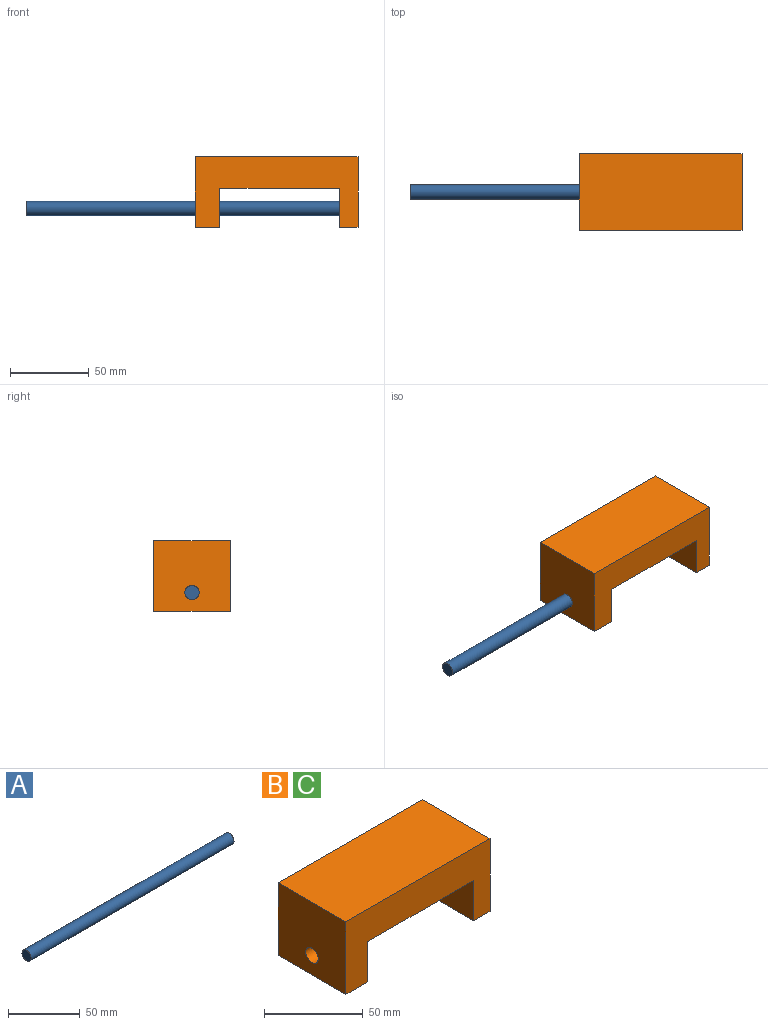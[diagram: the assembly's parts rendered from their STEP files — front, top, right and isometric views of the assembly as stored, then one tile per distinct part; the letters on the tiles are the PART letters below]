
ASSEMBLY  parts=3 mates=1
PART A: 3 faces, bbox 200x9x9 mm
  f0: cylinder r=4.5mm len=200mm, axis (1,0,0), area 5654.9mm2, adj f1,f2
  f1: plane 9x9mm, normal (-1,0,0), area 63.6mm2, adj f0
  f2: plane 9x9mm, normal (1,0,0), area 63.6mm2, adj f0
PART B: 11 faces, bbox 103.2x48.6x45 mm
  f0: plane 75.82x48.64mm, normal (0,0,-1), area 3687.7mm2, adj f1,f3,f6,f9
  f1: plane 103.2x45mm, normal (0,1,0), area 2748.6mm2, adj f0,f2,f4,f5,f6,f7,f9,f10
  f2: plane 48.64x45mm, normal (-1,0,0), area 2125mm2, adj f1,f3,f5,f7,f8
  f3: plane 103.2x45mm, normal (0,-1,0), area 2748.6mm2, adj f0,f2,f4,f5,f6,f7,f9,f10
  f4: plane 48.64x45mm, normal (1,0,0), area 2188.6mm2, adj f1,f3,f5,f10
  f5: plane 103.2x48.64mm, normal (0,0,1), area 5019.5mm2, adj f1,f2,f3,f4
  f6: plane 48.64x25mm, normal (1,0,0), area 1152.3mm2, adj f0,f1,f3,f7,f8
  f7: plane 48.64x15.58mm, normal (0,0,-1), area 757.7mm2, adj f1,f2,f3,f6
  f8: cylinder r=4.5mm len=15.58mm, axis (-1,0,0), area 440.5mm2, adj f2,f6
  f9: plane 48.64x25mm, normal (-1,0,0), area 1215.9mm2, adj f0,f1,f3,f10
  f10: plane 48.64x11.8mm, normal (0,0,-1), area 574.1mm2, adj f1,f3,f4,f9
PART C: same geometry as B
PLACE A rot(axis=(0,1,0),180deg) t=(-245.76,-22.4,-19.98)mm
PLACE B t=(-40.27,-22.4,6.01)mm
PLACE C t=(-40.27,-22.4,6.01)mm fixed
MATE slider C.f8 <-> A.f0  axis (1,0,0) through (-73.73,-19.43,-6.99)mm
